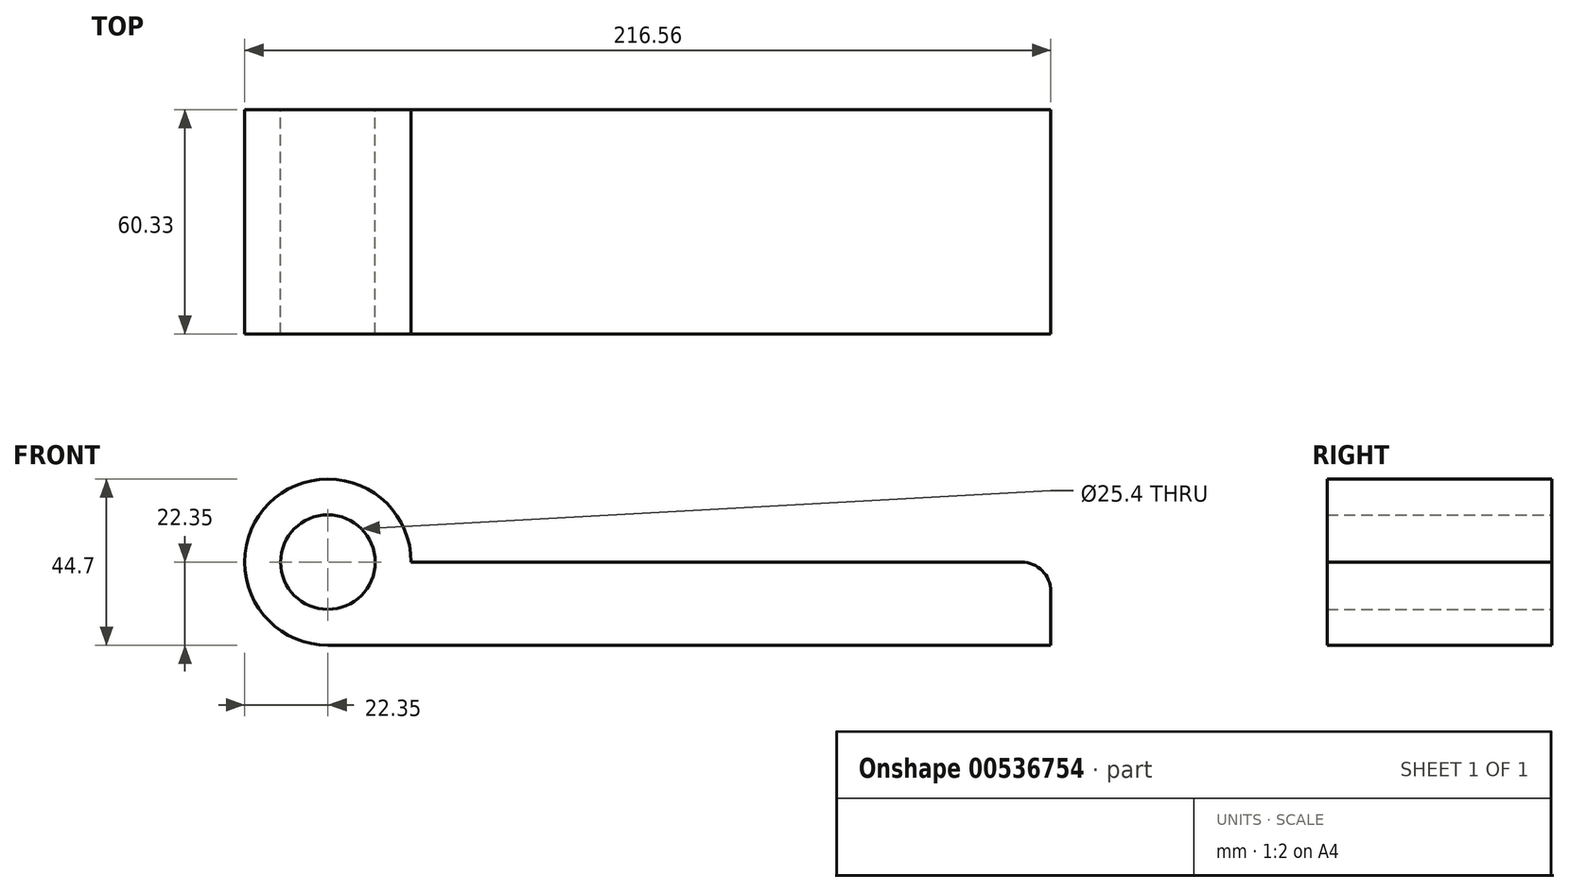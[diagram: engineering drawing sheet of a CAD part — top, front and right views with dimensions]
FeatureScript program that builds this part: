
annotation { "Feature Type Name" : "Feature", "Feature Type Description" : "" }
export const myFeature = defineFeature(function(context is Context, id is Id, definition is map)
    precondition{}
    {
        {
            var Q0;
            Q0=qCreatedBy(makeId("Front.planeOp"),FACE);
            var sketch = newSketch(context, id + "F0", { "sketchPlane" : qUnion([Q0])});
            skArc(sketch, "E0", {"start": v(22.35, 0) * mm, "mid": v(-15.8, 15.8) * mm, "end": v(0, -22.35) * mm});
            skCircle(sketch, "E1", {"center": v(0, 0) * mm, "radius": 12.7 * mm});
            skLineSegment(sketch, "E2", {"start": v(0, -22.35) * mm, "end": v(194.2, -22.35) * mm});
            skLineSegment(sketch, "E3", {"start": v(194.2, -22.35) * mm, "end": v(194.2, -7.87) * mm});
            skLineSegment(sketch, "E4", {"start": v(186.33, 0) * mm, "end": v(22.35, 0) * mm});
            skPoint(sketch, "E5.visualSharp", {"position": v(194.2, 0) * mm});
            skArc(sketch, "E5.filletArc", {"start": v(194.2, -7.87) * mm, "mid": v(191.9, -2.3) * mm, "end": v(186.33, 0) * mm});
            skSolve(sketch);
        }
        {
            var Q0;
            Q0=makeQuery(id+"F0.imprint","IMPRINT",FACE,{"disambiguationData":[TD([[makeQuery(id+"F0.imprint","IMPRINT",EDGE,{"derivedFrom":sQuery(id+"F0.wireOp",EDGE,"E0")}),1.0]])]});
            extrude(context, id + "F1", {"entities" : qUnion([Q0]), "depth" : 60.32 * mm, "offsetDistance" : 25.4 * mm});
        }
    });
